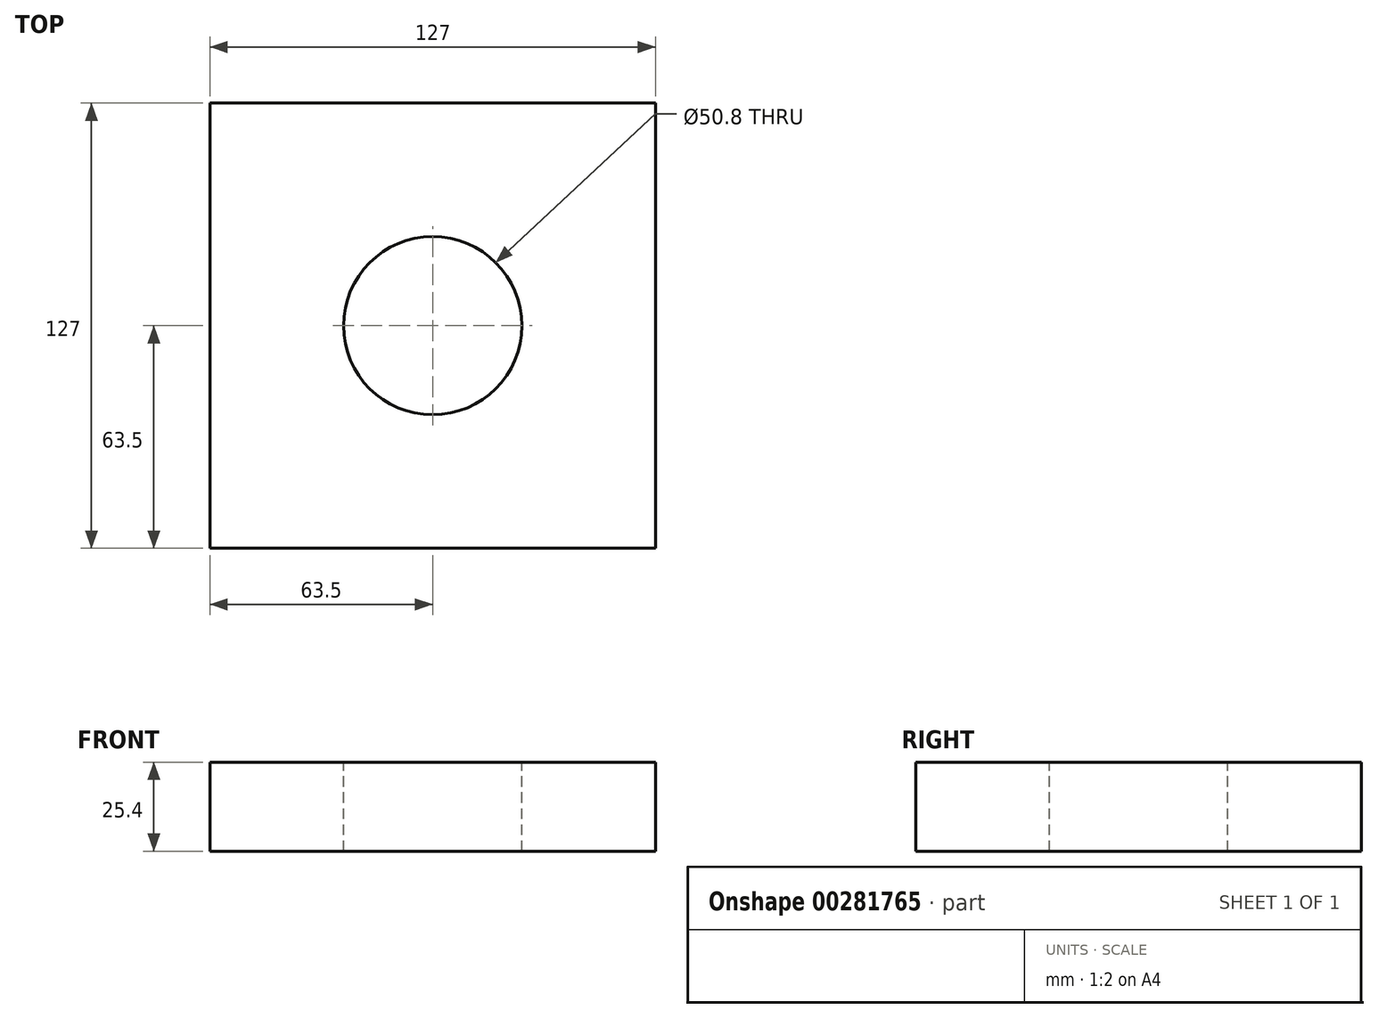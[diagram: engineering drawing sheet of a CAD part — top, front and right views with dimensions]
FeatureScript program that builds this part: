
annotation { "Feature Type Name" : "Feature", "Feature Type Description" : "" }
export const myFeature = defineFeature(function(context is Context, id is Id, definition is map)
    precondition{}
    {
        {
            var Q0;
            Q0=qCreatedBy(makeId("Front.planeOp"),FACE);
            var sketch = newSketch(context, id + "F0", { "sketchPlane" : qUnion([Q0])});
            skLineSegment(sketch, "E0.bottom", {"start": v(-63.5, 12.7) * mm, "end": v(63.5, 12.7) * mm});
            skLineSegment(sketch, "E0.top", {"start": v(-63.5, -12.7) * mm, "end": v(63.5, -12.7) * mm});
            skLineSegment(sketch, "E0.left", {"start": v(-63.5, 12.7) * mm, "end": v(-63.5, -12.7) * mm});
            skLineSegment(sketch, "E0.right", {"start": v(63.5, 12.7) * mm, "end": v(63.5, -12.7) * mm});
            skPoint(sketch, "E0.middle", {"position": v(0, 0) * mm});
            skSolve(sketch);
        }
        {
            var Q0;
            Q0 = qSketchRegion(id + "F0", true);
            extrude(context, id + "F1", {"entities" : qUnion([Q0]), "depth" : 127 * mm});
        }
        {
            var Q0;
            Q0=makeQuery(id+"F1.opExtrude","SWEPT_FACE",FACE,{"disambiguationData":[OSD([sQuery(id+"F0.wireOp",EDGE,"E0.bottom")])]});
            var sketch = newSketch(context, id + "F2", { "sketchPlane" : qUnion([Q0])});
            skCircle(sketch, "E1", {"center": v(0, -63.5) * mm, "radius": 25.4 * mm});
            skSolve(sketch);
        }
        {
            var Q0;
            Q0=sQuery(id+"F2.wireOp",VERTEX,"E1.center");
            var Q1;
            Q1=makeQuery(id+"F1.opExtrude","SWEPT_BODY",BODY,{"disambiguationData":[OSD([sQuery(id+"F0.wireOp",EDGE,"E0.bottom"),sQuery(id+"F0.wireOp",EDGE,"E0.top"),sQuery(id+"F0.wireOp",EDGE,"E0.left"),sQuery(id+"F0.wireOp",EDGE,"E0.right")])]});
            hole(context, id + "F3", {"style" : HoleStyle.SIMPLE, "endStyle" : HoleEndStyle.THROUGH, "holeDiameter" : 50.8 * mm, "tappedDepth" : 12.7 * mm, "tapClearance" : 3, "locations" : qUnion([Q0]), "scope" : qUnion([Q1])});
        }
    });
